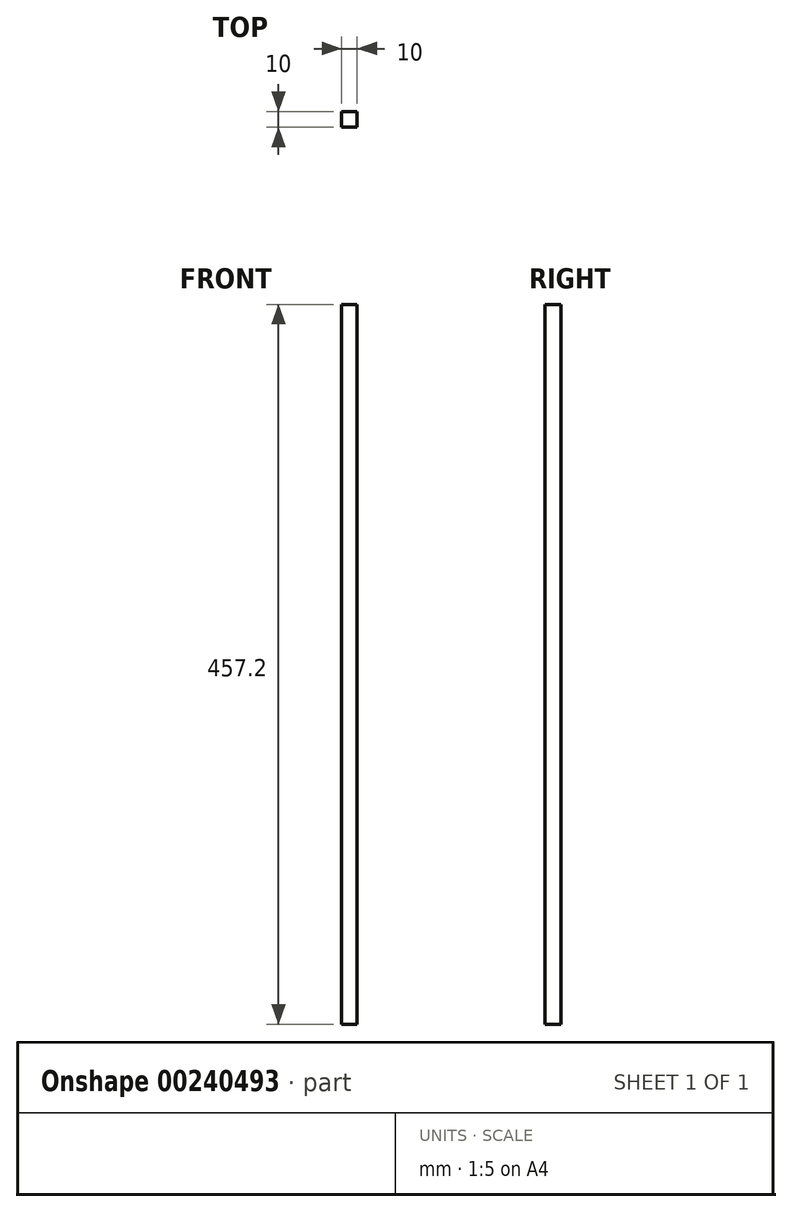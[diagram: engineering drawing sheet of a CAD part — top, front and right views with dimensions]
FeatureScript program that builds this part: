
annotation { "Feature Type Name" : "Feature", "Feature Type Description" : "" }
export const myFeature = defineFeature(function(context is Context, id is Id, definition is map)
    precondition{}
    {
        {
            var Q0;
            Q0=qCreatedBy(makeId("Front.planeOp"),FACE);
            var sketch = newSketch(context, id + "F0", { "sketchPlane" : qUnion([Q0])});
            skLineSegment(sketch, "E0.bottom", {"start": v(-84, 457.2) * mm, "end": v(-74, 457.2) * mm});
            skLineSegment(sketch, "E0.top", {"start": v(-84, 0) * mm, "end": v(-74, 0) * mm});
            skLineSegment(sketch, "E0.left", {"start": v(-84, 457.2) * mm, "end": v(-84, 0) * mm});
            skLineSegment(sketch, "E0.right", {"start": v(-74, 457.2) * mm, "end": v(-74, 0) * mm});
            skSolve(sketch);
        }
        {
            var Q0;
            Q0 = qSketchRegion(id + "F0", true);
            extrude(context, id + "F1", {"entities" : qUnion([Q0]), "depth" : 10 * mm});
        }
    });
